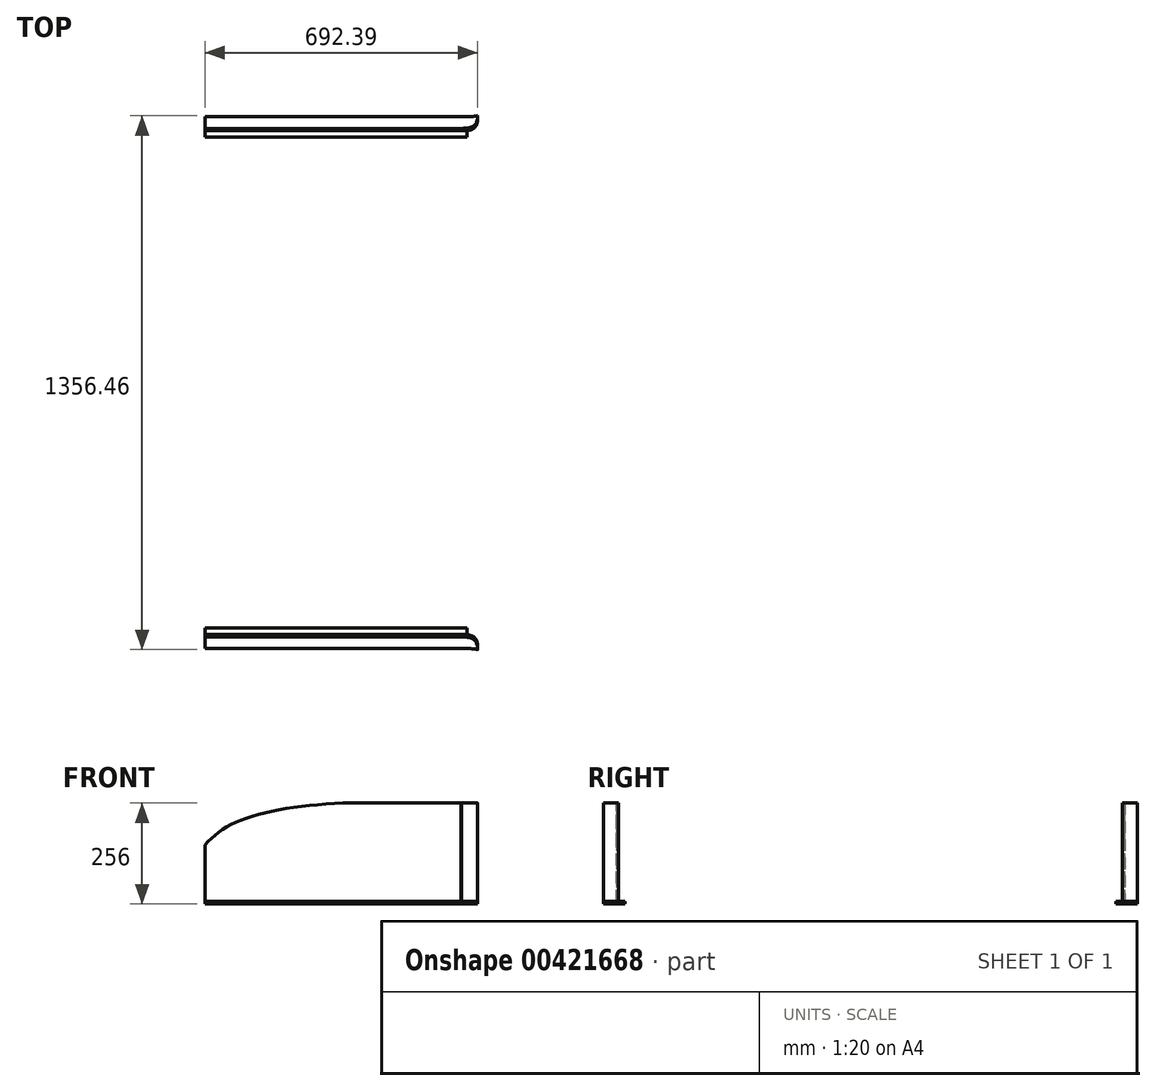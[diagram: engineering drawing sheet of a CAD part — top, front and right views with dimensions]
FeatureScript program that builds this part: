
annotation { "Feature Type Name" : "Feature", "Feature Type Description" : "" }
export const myFeature = defineFeature(function(context is Context, id is Id, definition is map)
    precondition{}
    {
        {
            var Q0;
            Q0=qCreatedBy(makeId("Front.planeOp"),FACE);
            cPlane(context, id + "F0", {"entities" : qUnion([Q0]), "cplaneType" : CPlaneType.OFFSET, "offset" : 640 * mm, "width" : 150 * mm, "height" : 150 * mm});
        }
        {
            var Q0;
            Q0=qCreatedBy(id+"F0.planeOp",FACE);
            var sketch = newSketch(context, id + "F1", { "sketchPlane" : qUnion([Q0])});
            skLineSegment(sketch, "E0", {"start": v(-895, 48) * mm, "end": v(-895, 298) * mm});
            skLineSegment(sketch, "E1", {"start": v(-895, 48) * mm, "end": v(-1545, 48) * mm});
            skLineSegment(sketch, "E2", {"start": v(-1545, 48) * mm, "end": v(-1545, 192) * mm});
            skLineSegment(sketch, "E3", {"start": v(-895, 298) * mm, "end": v(-1195, 298) * mm});
            skFitSpline(sketch, "E4", {"points": [v(-1545, 192) * mm, v(-1453.77, 254.87) * mm, v(-1195, 298) * mm], "startDerivative": vector(177.03, 202.62) * mm, "endDerivative": vector(499.8, 22.32) * mm});
            skSolve(sketch);
        }
        {
            var Q0;
            Q0=makeQuery(id+"F1.imprint","IMPRINT",FACE,{"disambiguationData":[TD([[makeQuery(id+"F1.imprint","IMPRINT",EDGE,{"derivedFrom":sQuery(id+"F1.wireOp",EDGE,"E0")}),1.0]])]});
            extrude(context, id + "F2", {"entities" : qUnion([Q0]), "depth" : 6 * mm});
        }
        {
            var Q0;
            Q0=makeQuery(id+"F2.opExtrude","SWEPT_FACE",FACE,{"disambiguationData":[OSD([sQuery(id+"F1.wireOp",EDGE,"E1")])]});
            cPlane(context, id + "F3", {"entities" : qUnion([Q0]), "cplaneType" : CPlaneType.OFFSET, "offset" : 0 * mm, "width" : 150 * mm, "height" : 150 * mm});
        }
        {
            var Q0;
            Q0=qCreatedBy(id+"F3.planeOp",FACE);
            var sketch = newSketch(context, id + "F4", { "sketchPlane" : qUnion([Q0])});
            skFitSpline(sketch, "E5", {"points": [v(-894.03, 639.92) * mm, v(-861.43, 647.2) * mm, v(-853, 678.22) * mm], "startDerivative": vector(88.49, 0.27) * mm, "endDerivative": vector(-6.95, 97.06) * mm});
            skFitSpline(sketch, "E6", {"points": [v(-894.11, 645.88) * mm, v(-865.74, 650.64) * mm, v(-853, 678.22) * mm], "startDerivative": vector(87.3, 2) * mm, "endDerivative": vector(3.56, 111.38) * mm});
            skLineSegment(sketch, "E7", {"start": v(-894.11, 645.88) * mm, "end": v(-894.03, 639.92) * mm});
            skSolve(sketch);
        }
        {
            var Q0;
            Q0=makeQuery(id+"F4.imprint","IMPRINT",FACE,{"disambiguationData":[TD([[makeQuery(id+"F4.imprint","IMPRINT",EDGE,{"derivedFrom":sQuery(id+"F4.wireOp",EDGE,"E5")}),1.0]])]});
            extrude(context, id + "F5", {"entities" : qUnion([Q0]), "operationType" : NewBodyOperationType.ADD, "oppositeDirection" : true, "depth" : 250 * mm});
        }
        {
            var Q1;
            Q1=makeQuery(id+"F2.opExtrude","SWEPT_FACE",FACE,{"disambiguationData":[OSD([sQuery(id+"F1.wireOp",EDGE,"E0")])]});
            var Q2;
            Q2=makeQuery(id+"F5.opExtrude","SWEPT_FACE",FACE,{"disambiguationData":[OSD([sQuery(id+"F4.wireOp",EDGE,"E7")])]});
            loft(context, id + "F6", {"operationType" : NewBodyOperationType.ADD, "sheetProfilesArray" : [{ "sheetProfileEntities" : qUnion([Q1]) }, { "sheetProfileEntities" : qUnion([Q2]) }]});
        }
        {
            var Q0;
            Q0=qCreatedBy(id+"F3.planeOp",FACE);
            var sketch = newSketch(context, id + "F7", { "sketchPlane" : qUnion([Q0])});
            skLineSegment(sketch, "E8.bottom", {"start": v(-1545.14, 623.84) * mm, "end": v(-879.86, 623.84) * mm});
            skLineSegment(sketch, "E8.top", {"start": v(-1545.14, 675.42) * mm, "end": v(-879.86, 675.42) * mm});
            skLineSegment(sketch, "E8.left", {"start": v(-1545.14, 623.84) * mm, "end": v(-1545.14, 675.42) * mm});
            skLineSegment(sketch, "E8.right", {"start": v(-879.86, 623.84) * mm, "end": v(-879.86, 640.77) * mm});
            skFitSpline(sketch, "E9", {"points": [v(-879.86, 675.42) * mm, v(-863.08, 676.47) * mm, v(-853.06, 678.23) * mm], "startDerivative": vector(31.78, 1.26) * mm, "endDerivative": vector(21.39, 4.48) * mm});
            skFitSpline(sketch, "E10", {"points": [v(-879.86, 640.77) * mm, v(-862.9, 645.99) * mm, v(-854.34, 659.22) * mm, v(-853.06, 678.23) * mm], "startDerivative": vector(54.9, 6.15) * mm, "endDerivative": vector(-2.48, 43.54) * mm});
            skSolve(sketch);
        }
        {
            var Q0;
            Q0=makeQuery(id+"F7.imprint","IMPRINT",FACE,{"disambiguationData":[TD([[makeQuery(id+"F7.imprint","IMPRINT",EDGE,{"derivedFrom":sQuery(id+"F7.wireOp",EDGE,"E8.bottom")}),1.0]])]});
            extrude(context, id + "F8", {"entities" : qUnion([Q0]), "operationType" : NewBodyOperationType.ADD, "depth" : 6 * mm});
        }
        {
            var Q0;
            Q0=makeQuery(id+"F2.opExtrude","SWEPT_BODY",BODY,{"disambiguationData":[OSD([sQuery(id+"F1.wireOp",EDGE,"E0"),sQuery(id+"F1.wireOp",EDGE,"E1"),sQuery(id+"F1.wireOp",EDGE,"E2"),sQuery(id+"F1.wireOp",EDGE,"E3"),sQuery(id+"F1.wireOp",EDGE,"E4")])]});
            var Q1;
            Q1=qCreatedBy(makeId("Front.planeOp"),FACE);
            mirror(context, id + "F9", {"entities" : qUnion([Q0]), "mirrorPlane" : qUnion([Q1])});
        }
    });
